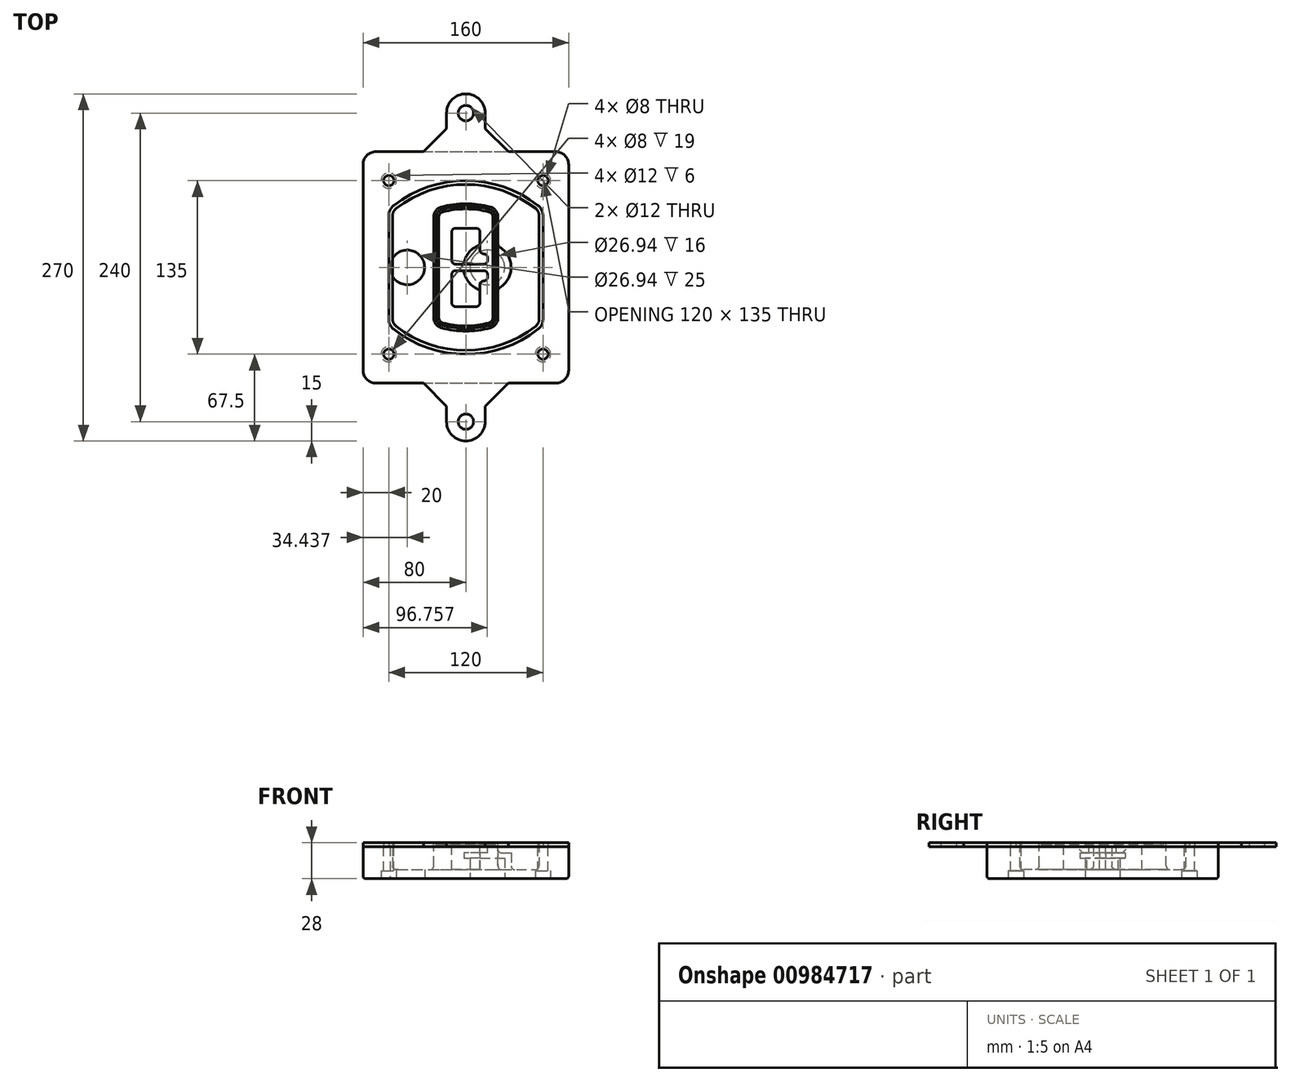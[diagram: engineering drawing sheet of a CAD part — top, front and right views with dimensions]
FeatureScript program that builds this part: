
annotation { "Feature Type Name" : "Feature", "Feature Type Description" : "" }
export const myFeature = defineFeature(function(context is Context, id is Id, definition is map)
    precondition{}
    {
        {
            var Q0;
            Q0=qCreatedBy(makeId("Top.planeOp"),FACE);
            var sketch = newSketch(context, id + "F0", { "sketchPlane" : qUnion([Q0])});
            skPoint(sketch, "E0.rect.middle", {"position": v(0, 0) * mm});
            skLineSegment(sketch, "E1.bottom", {"start": v(-70, -90) * mm, "end": v(70, -90) * mm});
            skLineSegment(sketch, "E1.top", {"start": v(-70, 90) * mm, "end": v(70, 90) * mm});
            skLineSegment(sketch, "E1.left", {"start": v(-80, -80) * mm, "end": v(-80, 80) * mm});
            skLineSegment(sketch, "E1.right", {"start": v(80, -80) * mm, "end": v(80, 80) * mm});
            skLineSegment(sketch, "E2", {"start": v(-80, 90) * mm, "end": v(80, -90) * mm, "construction": true});
            skLineSegment(sketch, "E3", {"start": v(80, 90) * mm, "end": v(-80, -90) * mm, "construction": true});
            skCircle(sketch, "E4", {"center": v(-60, 67.5) * mm, "radius": 4 * mm});
            skCircle(sketch, "E5", {"center": v(60, 67.5) * mm, "radius": 4 * mm});
            skCircle(sketch, "E6", {"center": v(60, -67.5) * mm, "radius": 4 * mm});
            skCircle(sketch, "E7", {"center": v(-60, -67.5) * mm, "radius": 4 * mm});
            skLineSegment(sketch, "E8", {"start": v(-60, 67.5) * mm, "end": v(60, 67.5) * mm, "construction": true});
            skLineSegment(sketch, "E9", {"start": v(60, 67.5) * mm, "end": v(60, -67.5) * mm, "construction": true});
            skLineSegment(sketch, "E10", {"start": v(60, -67.5) * mm, "end": v(-60, -67.5) * mm, "construction": true});
            skLineSegment(sketch, "E11", {"start": v(-60, -67.5) * mm, "end": v(-60, 67.5) * mm, "construction": true});
            skLineSegment(sketch, "E12", {"start": v(-60, 40.3) * mm, "end": v(-60, -40.3) * mm});
            skLineSegment(sketch, "E13", {"start": v(60, 40.3) * mm, "end": v(60, -40.3) * mm});
            skArc(sketch, "E14", {"start": v(56.15, 48.18) * mm, "mid": v(0, 67.5) * mm, "end": v(-56.15, 48.18) * mm});
            skArc(sketch, "E15", {"start": v(-56.15, -48.18) * mm, "mid": v(0, -67.5) * mm, "end": v(56.15, -48.18) * mm});
            skLineSegment(sketch, "E16", {"start": v(-60, 0) * mm, "end": v(60, 0) * mm, "construction": true});
            skPoint(sketch, "E17.visualSharp", {"position": v(-60, -45) * mm});
            skArc(sketch, "E17.filletArc", {"start": v(-60, -40.3) * mm, "mid": v(-58.99, -44.68) * mm, "end": v(-56.15, -48.18) * mm});
            skPoint(sketch, "E18.visualSharp", {"position": v(-60, 45) * mm});
            skArc(sketch, "E18.filletArc", {"start": v(-56.15, 48.18) * mm, "mid": v(-58.99, 44.68) * mm, "end": v(-60, 40.3) * mm});
            skPoint(sketch, "E19.visualSharp", {"position": v(60, 45) * mm});
            skArc(sketch, "E19.filletArc", {"start": v(60, 40.3) * mm, "mid": v(58.99, 44.68) * mm, "end": v(56.15, 48.18) * mm});
            skPoint(sketch, "E20.visualSharp", {"position": v(60, -45) * mm});
            skArc(sketch, "E20.filletArc", {"start": v(56.15, -48.18) * mm, "mid": v(58.99, -44.68) * mm, "end": v(60, -40.3) * mm});
            skPoint(sketch, "E21.visualSharp", {"position": v(-80, 90) * mm});
            skArc(sketch, "E21.filletArc", {"start": v(-70, 90) * mm, "mid": v(-77.07, 87.07) * mm, "end": v(-80, 80) * mm});
            skPoint(sketch, "E22.visualSharp", {"position": v(80, 90) * mm});
            skArc(sketch, "E22.filletArc", {"start": v(80, 80) * mm, "mid": v(77.07, 87.07) * mm, "end": v(70, 90) * mm});
            skPoint(sketch, "E23.visualSharp", {"position": v(80, -90) * mm});
            skArc(sketch, "E23.filletArc", {"start": v(70, -90) * mm, "mid": v(77.07, -87.07) * mm, "end": v(80, -80) * mm});
            skPoint(sketch, "E24.visualSharp", {"position": v(-80, -90) * mm});
            skArc(sketch, "E24.filletArc", {"start": v(-80, -80) * mm, "mid": v(-77.07, -87.07) * mm, "end": v(-70, -90) * mm});
            skArc(sketch, "E25.0", {"start": v(57, 40.3) * mm, "mid": v(56.3, 43.36) * mm, "end": v(54.3, 45.81) * mm});
            skLineSegment(sketch, "E25.1", {"start": v(57, 40.3) * mm, "end": v(57, -40.3) * mm});
            skArc(sketch, "E25.2", {"start": v(54.3, -45.81) * mm, "mid": v(56.3, -43.36) * mm, "end": v(57, -40.3) * mm});
            skArc(sketch, "E25.3", {"start": v(-54.3, -45.81) * mm, "mid": v(0, -64.5) * mm, "end": v(54.3, -45.81) * mm});
            skArc(sketch, "E25.4", {"start": v(-57, -40.3) * mm, "mid": v(-56.3, -43.36) * mm, "end": v(-54.3, -45.81) * mm});
            skArc(sketch, "E25.5", {"start": v(54.3, 45.81) * mm, "mid": v(0, 64.5) * mm, "end": v(-54.3, 45.81) * mm});
            skLineSegment(sketch, "E25.6", {"start": v(-57, 40.3) * mm, "end": v(-57, -40.3) * mm});
            skArc(sketch, "E25.7", {"start": v(-54.3, 45.81) * mm, "mid": v(-56.3, 43.36) * mm, "end": v(-57, 40.3) * mm});
            skArc(sketch, "E26.0", {"start": v(-58.62, 51.33) * mm, "mid": v(-62.58, 46.43) * mm, "end": v(-64, 40.3) * mm});
            skArc(sketch, "E26.1", {"start": v(58.62, 51.33) * mm, "mid": v(0, 71.5) * mm, "end": v(-58.62, 51.33) * mm});
            skArc(sketch, "E26.2", {"start": v(64, 40.3) * mm, "mid": v(62.58, 46.43) * mm, "end": v(58.62, 51.33) * mm});
            skLineSegment(sketch, "E26.3", {"start": v(64, 40.3) * mm, "end": v(64, -40.3) * mm});
            skArc(sketch, "E26.4", {"start": v(58.62, -51.33) * mm, "mid": v(62.58, -46.43) * mm, "end": v(64, -40.3) * mm});
            skLineSegment(sketch, "E26.5", {"start": v(-64, 40.3) * mm, "end": v(-64, -40.3) * mm});
            skArc(sketch, "E26.6", {"start": v(-58.62, -51.33) * mm, "mid": v(0, -71.5) * mm, "end": v(58.62, -51.33) * mm});
            skArc(sketch, "E26.7", {"start": v(-64, -40.3) * mm, "mid": v(-62.58, -46.43) * mm, "end": v(-58.62, -51.33) * mm});
            skSolve(sketch);
        }
        {
            var Q0;
            Q0=makeQuery(id+"F0.imprint","IMPRINT",FACE,{"disambiguationData":[TD([[makeQuery(id+"F0.imprint","IMPRINT",EDGE,{"derivedFrom":sQuery(id+"F0.wireOp",EDGE,"E1.bottom")}),1.0]])]});
            var Q1;
            Q1=makeQuery(id+"F0.imprint","IMPRINT",FACE,{"disambiguationData":[TD([[makeQuery(id+"F0.imprint","IMPRINT",EDGE,{"derivedFrom":sQuery(id+"F0.wireOp",EDGE,"E12")}),1.0]])]});
            var Q2;
            Q2=makeQuery(id+"F0.imprint","IMPRINT",FACE,{"disambiguationData":[TD([[makeQuery(id+"F0.imprint","IMPRINT",EDGE,{"derivedFrom":sQuery(id+"F0.wireOp",EDGE,"E25.0")}),1.0]])]});
            var Q3;
            Q3=makeQuery(id+"F0.imprint","IMPRINT",FACE,{"disambiguationData":[TD([[makeQuery(id+"F0.imprint","IMPRINT",EDGE,{"derivedFrom":sQuery(id+"F0.wireOp",EDGE,"E12")}),-1.0]])]});
            extrude(context, id + "F1", {"entities" : qUnion([Q0, Q1, Q2, Q3]), "oppositeDirection" : true, "depth" : 25 * mm});
        }
        {
            var Q0;
            Q0=makeQuery(id+"F0.imprint","IMPRINT",FACE,{"disambiguationData":[TD([[makeQuery(id+"F0.imprint","IMPRINT",EDGE,{"derivedFrom":sQuery(id+"F0.wireOp",EDGE,"E12")}),1.0]])]});
            extrude(context, id + "F2", {"entities" : qUnion([Q0]), "operationType" : NewBodyOperationType.ADD, "depth" : 3 * mm});
        }
        {
            var Q0;
            Q0=makeQuery(id+"F0.imprint","IMPRINT",FACE,{"disambiguationData":[TD([[makeQuery(id+"F0.imprint","IMPRINT",EDGE,{"derivedFrom":sQuery(id+"F0.wireOp",EDGE,"E25.0")}),1.0]])]});
            extrude(context, id + "F3", {"entities" : qUnion([Q0]), "operationType" : NewBodyOperationType.REMOVE, "oppositeDirection" : true, "depth" : 18 * mm});
        }
        {
            var Q0;
            Q0=makeQuery(id+"F2.opExtrude","CAP_FACE",FACE,{"disambiguationData":[OSD([sQuery(id+"F0.wireOp",EDGE,"E12"),sQuery(id+"F0.wireOp",EDGE,"E13"),sQuery(id+"F0.wireOp",EDGE,"E14"),sQuery(id+"F0.wireOp",EDGE,"E15"),sQuery(id+"F0.wireOp",EDGE,"E17.filletArc"),sQuery(id+"F0.wireOp",EDGE,"E18.filletArc"),sQuery(id+"F0.wireOp",EDGE,"E19.filletArc"),sQuery(id+"F0.wireOp",EDGE,"E20.filletArc"),sQuery(id+"F0.wireOp",EDGE,"E25.0"),sQuery(id+"F0.wireOp",EDGE,"E25.1"),sQuery(id+"F0.wireOp",EDGE,"E25.2"),sQuery(id+"F0.wireOp",EDGE,"E25.3"),sQuery(id+"F0.wireOp",EDGE,"E25.4"),sQuery(id+"F0.wireOp",EDGE,"E25.5"),sQuery(id+"F0.wireOp",EDGE,"E25.6"),sQuery(id+"F0.wireOp",EDGE,"E25.7")])],"isStart":false});
            var sketch = newSketch(context, id + "F4", { "sketchPlane" : qUnion([Q0])});
            skArc(sketch, "E27.0", {"start": v(-19.08, -46.97) * mm, "mid": v(0, -49.5) * mm, "end": v(19.08, -46.97) * mm});
            skArc(sketch, "E28.0", {"start": v(19.08, 46.97) * mm, "mid": v(0, 49.5) * mm, "end": v(-19.08, 46.97) * mm});
            skLineSegment(sketch, "E29", {"start": v(-25, 39.25) * mm, "end": v(-25, -39.25) * mm});
            skLineSegment(sketch, "E30", {"start": v(25, 39.25) * mm, "end": v(25, -39.25) * mm});
            skLineSegment(sketch, "E31", {"start": v(-25, 45.1) * mm, "end": v(25, 45.1) * mm, "construction": true});
            skLineSegment(sketch, "E32", {"start": v(-25, -45.1) * mm, "end": v(25, -45.1) * mm, "construction": true});
            skPoint(sketch, "E33.visualSharp", {"position": v(-25, 45.1) * mm});
            skArc(sketch, "E33.filletArc", {"start": v(-19.08, 46.97) * mm, "mid": v(-23.35, 44.11) * mm, "end": v(-25, 39.25) * mm});
            skPoint(sketch, "E34.visualSharp", {"position": v(25, 45.1) * mm});
            skArc(sketch, "E34.filletArc", {"start": v(25, 39.25) * mm, "mid": v(23.35, 44.11) * mm, "end": v(19.08, 46.97) * mm});
            skPoint(sketch, "E35.visualSharp", {"position": v(25, -45.1) * mm});
            skArc(sketch, "E35.filletArc", {"start": v(19.08, -46.97) * mm, "mid": v(23.35, -44.11) * mm, "end": v(25, -39.25) * mm});
            skPoint(sketch, "E36.visualSharp", {"position": v(-25, -45.1) * mm});
            skArc(sketch, "E36.filletArc", {"start": v(-25, -39.25) * mm, "mid": v(-23.35, -44.11) * mm, "end": v(-19.08, -46.97) * mm});
            skArc(sketch, "E37.0", {"start": v(54.3, 45.81) * mm, "mid": v(0, 64.5) * mm, "end": v(-54.3, 45.81) * mm});
            skArc(sketch, "E37.1", {"start": v(-54.3, 45.81) * mm, "mid": v(-56.3, 43.36) * mm, "end": v(-57, 40.3) * mm});
            skLineSegment(sketch, "E37.2", {"start": v(-57, 40.3) * mm, "end": v(-57, -40.3) * mm});
            skArc(sketch, "E37.3", {"start": v(-57, -40.3) * mm, "mid": v(-56.3, -43.36) * mm, "end": v(-54.3, -45.81) * mm});
            skArc(sketch, "E37.4", {"start": v(-54.3, -45.81) * mm, "mid": v(0, -64.5) * mm, "end": v(54.3, -45.81) * mm});
            skArc(sketch, "E37.5", {"start": v(54.3, -45.81) * mm, "mid": v(56.3, -43.36) * mm, "end": v(57, -40.3) * mm});
            skLineSegment(sketch, "E37.6", {"start": v(57, 40.3) * mm, "end": v(57, -40.3) * mm});
            skArc(sketch, "E37.7", {"start": v(57, 40.3) * mm, "mid": v(56.3, 43.36) * mm, "end": v(54.3, 45.81) * mm});
            skLineSegment(sketch, "E38.0", {"start": v(23, 39.25) * mm, "end": v(23, -39.25) * mm});
            skArc(sketch, "E38.1", {"start": v(18.56, -45.04) * mm, "mid": v(21.76, -42.9) * mm, "end": v(23, -39.25) * mm});
            skArc(sketch, "E38.2", {"start": v(-18.56, -45.04) * mm, "mid": v(0, -47.5) * mm, "end": v(18.56, -45.04) * mm});
            skArc(sketch, "E38.3", {"start": v(-23, -39.25) * mm, "mid": v(-21.76, -42.9) * mm, "end": v(-18.56, -45.04) * mm});
            skLineSegment(sketch, "E38.4", {"start": v(-23, 39.25) * mm, "end": v(-23, -39.25) * mm});
            skArc(sketch, "E38.5", {"start": v(23, 39.25) * mm, "mid": v(21.76, 42.9) * mm, "end": v(18.56, 45.04) * mm});
            skArc(sketch, "E38.6", {"start": v(-18.56, 45.04) * mm, "mid": v(-21.76, 42.9) * mm, "end": v(-23, 39.25) * mm});
            skArc(sketch, "E38.7", {"start": v(18.56, 45.04) * mm, "mid": v(0, 47.5) * mm, "end": v(-18.56, 45.04) * mm});
            skArc(sketch, "E39.0", {"start": v(21, 39.25) * mm, "mid": v(20.18, 41.68) * mm, "end": v(18.04, 43.1) * mm});
            skLineSegment(sketch, "E39.1", {"start": v(21, 39.25) * mm, "end": v(21, -39.25) * mm});
            skArc(sketch, "E39.2", {"start": v(18.04, -43.1) * mm, "mid": v(20.18, -41.68) * mm, "end": v(21, -39.25) * mm});
            skArc(sketch, "E39.3", {"start": v(-18.04, -43.1) * mm, "mid": v(0, -45.5) * mm, "end": v(18.04, -43.1) * mm});
            skArc(sketch, "E39.4", {"start": v(-21, -39.25) * mm, "mid": v(-20.18, -41.68) * mm, "end": v(-18.04, -43.1) * mm});
            skArc(sketch, "E39.5", {"start": v(18.04, 43.1) * mm, "mid": v(0, 45.5) * mm, "end": v(-18.04, 43.1) * mm});
            skLineSegment(sketch, "E39.6", {"start": v(-21, 39.25) * mm, "end": v(-21, -39.25) * mm});
            skArc(sketch, "E39.7", {"start": v(-18.04, 43.1) * mm, "mid": v(-20.18, 41.68) * mm, "end": v(-21, 39.25) * mm});
            skLineSegment(sketch, "E40", {"start": v(-25, 0) * mm, "end": v(25, 0) * mm, "construction": true});
            skLineSegment(sketch, "E41", {"start": v(-11, 5.5) * mm, "end": v(-11, 27.5) * mm});
            skLineSegment(sketch, "E42", {"start": v(-8, 30.5) * mm, "end": v(8, 30.5) * mm});
            skLineSegment(sketch, "E43", {"start": v(11, 27.5) * mm, "end": v(11, 13.5) * mm});
            skLineSegment(sketch, "E44", {"start": v(14, 10.5) * mm, "end": v(14, 10.5) * mm});
            skLineSegment(sketch, "E45", {"start": v(17, 7.5) * mm, "end": v(17, 5.5) * mm});
            skLineSegment(sketch, "E46", {"start": v(14, 2.5) * mm, "end": v(-8, 2.5) * mm});
            skPoint(sketch, "E47.visualSharp", {"position": v(-11, 30.5) * mm});
            skArc(sketch, "E47.filletArc", {"start": v(-8, 30.5) * mm, "mid": v(-10.12, 29.62) * mm, "end": v(-11, 27.5) * mm});
            skPoint(sketch, "E48.visualSharp", {"position": v(11, 30.5) * mm});
            skArc(sketch, "E48.filletArc", {"start": v(11, 27.5) * mm, "mid": v(10.12, 29.62) * mm, "end": v(8, 30.5) * mm});
            skPoint(sketch, "E49.visualSharp", {"position": v(11, 10.5) * mm});
            skArc(sketch, "E49.filletArc", {"start": v(11, 13.5) * mm, "mid": v(11.88, 11.38) * mm, "end": v(14, 10.5) * mm});
            skPoint(sketch, "E50.visualSharp", {"position": v(17, 10.5) * mm});
            skArc(sketch, "E50.filletArc", {"start": v(17, 7.5) * mm, "mid": v(16.12, 9.62) * mm, "end": v(14, 10.5) * mm});
            skPoint(sketch, "E51.visualSharp", {"position": v(17, 2.5) * mm});
            skArc(sketch, "E51.filletArc", {"start": v(14, 2.5) * mm, "mid": v(16.12, 3.38) * mm, "end": v(17, 5.5) * mm});
            skPoint(sketch, "E52.visualSharp", {"position": v(-11, 2.5) * mm});
            skArc(sketch, "E52.filletArc", {"start": v(-11, 5.5) * mm, "mid": v(-10.12, 3.38) * mm, "end": v(-8, 2.5) * mm});
            skLineSegment(sketch, "E53.0.MirrorCS", {"start": v(14, -2.5) * mm, "end": v(-8, -2.5) * mm});
            skArc(sketch, "E54.0.MirrorCS", {"start": v(-11, -5.5) * mm, "mid": v(-10.12, -3.38) * mm, "end": v(-8, -2.5) * mm});
            skLineSegment(sketch, "E55.0.MirrorCS", {"start": v(-11, -5.5) * mm, "end": v(-11, -27.5) * mm});
            skArc(sketch, "E56.0.MirrorCS", {"start": v(-8, -30.5) * mm, "mid": v(-10.12, -29.62) * mm, "end": v(-11, -27.5) * mm});
            skLineSegment(sketch, "E57.0.MirrorCS", {"start": v(-8, -30.5) * mm, "end": v(8, -30.5) * mm});
            skArc(sketch, "E58.0.MirrorCS", {"start": v(11, -27.5) * mm, "mid": v(10.12, -29.62) * mm, "end": v(8, -30.5) * mm});
            skLineSegment(sketch, "E59.0.MirrorCS", {"start": v(11, -27.5) * mm, "end": v(11, -13.5) * mm});
            skArc(sketch, "E60.0.MirrorCS", {"start": v(11, -13.5) * mm, "mid": v(11.88, -11.38) * mm, "end": v(14, -10.5) * mm});
            skArc(sketch, "E61.0.MirrorCS", {"start": v(17, -7.5) * mm, "mid": v(16.12, -9.62) * mm, "end": v(14, -10.5) * mm});
            skLineSegment(sketch, "E62.0.MirrorCS", {"start": v(17, -7.5) * mm, "end": v(17, -5.5) * mm});
            skArc(sketch, "E63.0.MirrorCS", {"start": v(14, -2.5) * mm, "mid": v(16.12, -3.38) * mm, "end": v(17, -5.5) * mm});
            skSolve(sketch);
        }
        {
            var Q0;
            Q0=makeQuery(id+"F4.imprint","IMPRINT",FACE,{"disambiguationData":[TD([[makeQuery(id+"F4.imprint","IMPRINT",EDGE,{"derivedFrom":sQuery(id+"F4.wireOp",EDGE,"E27.0")}),1.0]])]});
            var Q1;
            Q1=makeQuery(id+"F4.imprint","IMPRINT",FACE,{"disambiguationData":[TD([[makeQuery(id+"F4.imprint","IMPRINT",EDGE,{"derivedFrom":sQuery(id+"F4.wireOp",EDGE,"E38.0")}),-1.0]])]});
            var Q2;
            Q2=makeQuery(id+"F4.imprint","IMPRINT",FACE,{"disambiguationData":[TD([[makeQuery(id+"F4.imprint","IMPRINT",EDGE,{"derivedFrom":sQuery(id+"F4.wireOp",EDGE,"E39.0")}),1.0]])]});
            extrude(context, id + "F5", {"entities" : qUnion([Q0, Q1, Q2]), "operationType" : NewBodyOperationType.ADD, "endBound" : BoundingType.UP_TO_NEXT, "oppositeDirection" : true, "depth" : 25 * mm});
        }
        {
            var Q0;
            Q0=makeQuery(id+"F4.imprint","IMPRINT",FACE,{"disambiguationData":[TD([[makeQuery(id+"F4.imprint","IMPRINT",EDGE,{"derivedFrom":sQuery(id+"F4.wireOp",EDGE,"E38.0")}),-1.0]])]});
            extrude(context, id + "F6", {"entities" : qUnion([Q0]), "operationType" : NewBodyOperationType.REMOVE, "oppositeDirection" : true, "depth" : 2 * mm});
        }
        {
            var Q0;
            Q0=makeQuery(id+"F1.opExtrude","CAP_FACE",FACE,{"disambiguationData":[OSD([sQuery(id+"F0.wireOp",EDGE,"E1.bottom"),sQuery(id+"F0.wireOp",EDGE,"E1.top"),sQuery(id+"F0.wireOp",EDGE,"E1.left"),sQuery(id+"F0.wireOp",EDGE,"E1.right"),sQuery(id+"F0.wireOp",EDGE,"E4"),sQuery(id+"F0.wireOp",EDGE,"E5"),sQuery(id+"F0.wireOp",EDGE,"E6"),sQuery(id+"F0.wireOp",EDGE,"E7"),sQuery(id+"F0.wireOp",EDGE,"E21.filletArc"),sQuery(id+"F0.wireOp",EDGE,"E22.filletArc"),sQuery(id+"F0.wireOp",EDGE,"E23.filletArc"),sQuery(id+"F0.wireOp",EDGE,"E24.filletArc")])],"isStart":false});
            var sketch = newSketch(context, id + "F7", { "sketchPlane" : qUnion([Q0])});
            skCircle(sketch, "E64", {"center": v(16.76, 0) * mm, "radius": 13.47 * mm});
            skCircle(sketch, "E65", {"center": v(-45.56, 0) * mm, "radius": 13.47 * mm});
            skLineSegment(sketch, "E66", {"start": v(80, 0) * mm, "end": v(-80, 0) * mm});
            skCircle(sketch, "E67", {"center": v(16.76, 0) * mm, "radius": 18.47 * mm});
            skCircle(sketch, "E68", {"center": v(60, -67.5) * mm, "radius": 6 * mm});
            skCircle(sketch, "E69", {"center": v(-60, -67.5) * mm, "radius": 6 * mm});
            skCircle(sketch, "E70", {"center": v(-60, 67.5) * mm, "radius": 6 * mm});
            skCircle(sketch, "E71", {"center": v(60, 67.5) * mm, "radius": 6 * mm});
            skSolve(sketch);
        }
        {
            var Q0;
            {var subQ1=sQuery(id+"F7.wireOp",EDGE,"E66");var subQ4=sQuery(id+"F7.wireOp",EDGE,"E64");var subQ6=makeQuery(id+"F7.imprint","INTERSECT",VERTEX,{"disambiguationData":[OD(0.0)],"derivedFrom":[subQ4,subQ1]});Q0=makeQuery(id+"F7.imprint","IMPRINT",FACE,{"disambiguationData":[TD([[makeQuery(id+"F7.imprint","IMPRINT",EDGE,{"disambiguationData":[TD([[subQ6,-1.0]])],"derivedFrom":subQ4}),-1.0]])]});}
            var Q1;
            {var subQ0=sQuery(id+"F7.wireOp",EDGE,"E66");var subQ1=sQuery(id+"F7.wireOp",EDGE,"E64");var subQ3=makeQuery(id+"F7.imprint","INTERSECT",VERTEX,{"disambiguationData":[OD(0.0)],"derivedFrom":[subQ1,subQ0]});Q1=makeQuery(id+"F7.imprint","IMPRINT",FACE,{"disambiguationData":[TD([[makeQuery(id+"F7.imprint","IMPRINT",EDGE,{"disambiguationData":[TD([[subQ3,-1.0]])],"derivedFrom":subQ1}),1.0]])]});}
            var Q2;
            {var subQ0=sQuery(id+"F7.wireOp",EDGE,"E66");var subQ1=sQuery(id+"F7.wireOp",EDGE,"E64");var subQ3=makeQuery(id+"F7.imprint","INTERSECT",VERTEX,{"disambiguationData":[OD(0.0)],"derivedFrom":[subQ1,subQ0]});Q2=makeQuery(id+"F7.imprint","IMPRINT",FACE,{"disambiguationData":[TD([[makeQuery(id+"F7.imprint","IMPRINT",EDGE,{"disambiguationData":[TD([[subQ3,1.0]])],"derivedFrom":subQ1}),1.0]])]});}
            var Q3;
            {var subQ1=sQuery(id+"F7.wireOp",EDGE,"E66");var subQ4=sQuery(id+"F7.wireOp",EDGE,"E64");var subQ6=makeQuery(id+"F7.imprint","INTERSECT",VERTEX,{"disambiguationData":[OD(0.0)],"derivedFrom":[subQ4,subQ1]});Q3=makeQuery(id+"F7.imprint","IMPRINT",FACE,{"disambiguationData":[TD([[makeQuery(id+"F7.imprint","IMPRINT",EDGE,{"disambiguationData":[TD([[subQ6,1.0]])],"derivedFrom":subQ4}),-1.0]])]});}
            extrude(context, id + "F8", {"entities" : qUnion([Q0, Q1, Q2, Q3]), "operationType" : NewBodyOperationType.ADD, "oppositeDirection" : true, "depth" : 20 * mm});
        }
        {
            var Q0;
            {var subQ0=sQuery(id+"F7.wireOp",EDGE,"E66");var subQ1=sQuery(id+"F7.wireOp",EDGE,"E64");var subQ3=makeQuery(id+"F7.imprint","INTERSECT",VERTEX,{"disambiguationData":[OD(0.0)],"derivedFrom":[subQ1,subQ0]});Q0=makeQuery(id+"F7.imprint","IMPRINT",FACE,{"disambiguationData":[TD([[makeQuery(id+"F7.imprint","IMPRINT",EDGE,{"disambiguationData":[TD([[subQ3,-1.0]])],"derivedFrom":subQ1}),1.0]])]});}
            var Q1;
            {var subQ0=sQuery(id+"F7.wireOp",EDGE,"E66");var subQ1=sQuery(id+"F7.wireOp",EDGE,"E64");var subQ3=makeQuery(id+"F7.imprint","INTERSECT",VERTEX,{"disambiguationData":[OD(0.0)],"derivedFrom":[subQ1,subQ0]});Q1=makeQuery(id+"F7.imprint","IMPRINT",FACE,{"disambiguationData":[TD([[makeQuery(id+"F7.imprint","IMPRINT",EDGE,{"disambiguationData":[TD([[subQ3,1.0]])],"derivedFrom":subQ1}),1.0]])]});}
            extrude(context, id + "F9", {"entities" : qUnion([Q0, Q1]), "operationType" : NewBodyOperationType.REMOVE, "oppositeDirection" : true, "depth" : 16 * mm});
        }
        {
            var Q0;
            {var subQ0=sQuery(id+"F7.wireOp",EDGE,"E66");var subQ1=sQuery(id+"F7.wireOp",EDGE,"E65");var subQ3=makeQuery(id+"F7.imprint","INTERSECT",VERTEX,{"disambiguationData":[OD(0.0)],"derivedFrom":[subQ1,subQ0]});Q0=makeQuery(id+"F7.imprint","IMPRINT",FACE,{"disambiguationData":[TD([[makeQuery(id+"F7.imprint","IMPRINT",EDGE,{"disambiguationData":[TD([[subQ3,-1.0]])],"derivedFrom":subQ1}),1.0]])]});}
            var Q1;
            {var subQ0=sQuery(id+"F7.wireOp",EDGE,"E66");var subQ1=sQuery(id+"F7.wireOp",EDGE,"E65");var subQ3=makeQuery(id+"F7.imprint","INTERSECT",VERTEX,{"disambiguationData":[OD(0.0)],"derivedFrom":[subQ1,subQ0]});Q1=makeQuery(id+"F7.imprint","IMPRINT",FACE,{"disambiguationData":[TD([[makeQuery(id+"F7.imprint","IMPRINT",EDGE,{"disambiguationData":[TD([[subQ3,1.0]])],"derivedFrom":subQ1}),1.0]])]});}
            extrude(context, id + "F10", {"entities" : qUnion([Q0, Q1]), "operationType" : NewBodyOperationType.REMOVE, "oppositeDirection" : true, "depth" : 25 * mm});
        }
        {
            var Q0;
            Q0=makeQuery(id+"F7.imprint","IMPRINT",FACE,{"disambiguationData":[TD([[makeQuery(id+"F7.imprint","IMPRINT",EDGE,{"derivedFrom":sQuery(id+"F7.wireOp",EDGE,"E68")}),1.0]])]});
            var Q1;
            Q1=makeQuery(id+"F7.imprint","IMPRINT",FACE,{"disambiguationData":[TD([[makeQuery(id+"F7.imprint","IMPRINT",EDGE,{"derivedFrom":makeQuery(id+"F1.opExtrude","CAP_EDGE",EDGE,{"disambiguationData":[OSD([sQuery(id+"F0.wireOp",EDGE,"E5")])],"isStart":false})}),-1.0]])]});
            var Q2;
            Q2=makeQuery(id+"F7.imprint","IMPRINT",FACE,{"disambiguationData":[TD([[makeQuery(id+"F7.imprint","IMPRINT",EDGE,{"derivedFrom":sQuery(id+"F7.wireOp",EDGE,"E69")}),1.0]])]});
            var Q3;
            Q3=makeQuery(id+"F7.imprint","IMPRINT",FACE,{"disambiguationData":[TD([[makeQuery(id+"F7.imprint","IMPRINT",EDGE,{"derivedFrom":makeQuery(id+"F1.opExtrude","CAP_EDGE",EDGE,{"disambiguationData":[OSD([sQuery(id+"F0.wireOp",EDGE,"E4")])],"isStart":false})}),-1.0]])]});
            var Q4;
            Q4=makeQuery(id+"F7.imprint","IMPRINT",FACE,{"disambiguationData":[TD([[makeQuery(id+"F7.imprint","IMPRINT",EDGE,{"derivedFrom":sQuery(id+"F7.wireOp",EDGE,"E70")}),1.0]])]});
            var Q5;
            Q5=makeQuery(id+"F7.imprint","IMPRINT",FACE,{"disambiguationData":[TD([[makeQuery(id+"F7.imprint","IMPRINT",EDGE,{"derivedFrom":makeQuery(id+"F1.opExtrude","CAP_EDGE",EDGE,{"disambiguationData":[OSD([sQuery(id+"F0.wireOp",EDGE,"E7")])],"isStart":false})}),-1.0]])]});
            var Q6;
            Q6=makeQuery(id+"F7.imprint","IMPRINT",FACE,{"disambiguationData":[TD([[makeQuery(id+"F7.imprint","IMPRINT",EDGE,{"derivedFrom":sQuery(id+"F7.wireOp",EDGE,"E71")}),1.0]])]});
            var Q7;
            Q7=makeQuery(id+"F7.imprint","IMPRINT",FACE,{"disambiguationData":[TD([[makeQuery(id+"F7.imprint","IMPRINT",EDGE,{"derivedFrom":makeQuery(id+"F1.opExtrude","CAP_EDGE",EDGE,{"disambiguationData":[OSD([sQuery(id+"F0.wireOp",EDGE,"E6")])],"isStart":false})}),-1.0]])]});
            extrude(context, id + "F11", {"entities" : qUnion([Q0, Q1, Q2, Q3, Q4, Q5, Q6, Q7]), "operationType" : NewBodyOperationType.REMOVE, "oppositeDirection" : true, "depth" : 6 * mm});
        }
        {
            var Q0;
            Q0=makeQuery(id+"F9.boolean.opBoolean","COPY",FACE,{"derivedFrom":makeQuery(id+"F9.opExtrude","CAP_FACE",FACE,{"disambiguationData":[OSD([sQuery(id+"F7.wireOp",EDGE,"E64")])],"isStart":false})});
            var sketch = newSketch(context, id + "F12", { "sketchPlane" : qUnion([Q0])});
            skArc(sketch, "E72.0", {"start": v(11, 17.55) * mm, "mid": v(2.57, 11.82) * mm, "end": v(-1.54, 2.5) * mm});
            skArc(sketch, "E72.1", {"start": v(-1.54, -2.5) * mm, "mid": v(2.57, -11.82) * mm, "end": v(11, -17.55) * mm});
            skLineSegment(sketch, "E73", {"start": v(-1.54, -2.5) * mm, "end": v(14, -2.5) * mm});
            skLineSegment(sketch, "E74.0", {"start": v(14, 2.5) * mm, "end": v(-1.54, 2.5) * mm});
            skArc(sketch, "E74.1", {"start": v(14, 2.5) * mm, "mid": v(16.12, 3.38) * mm, "end": v(17, 5.5) * mm});
            skLineSegment(sketch, "E74.2", {"start": v(17, 7.5) * mm, "end": v(17, 5.5) * mm});
            skArc(sketch, "E74.3", {"start": v(17, 7.5) * mm, "mid": v(16.12, 9.62) * mm, "end": v(14, 10.5) * mm});
            skArc(sketch, "E74.4", {"start": v(11, 13.5) * mm, "mid": v(11.88, 11.38) * mm, "end": v(14, 10.5) * mm});
            skLineSegment(sketch, "E74.5", {"start": v(11, 17.55) * mm, "end": v(11, 13.5) * mm});
            skLineSegment(sketch, "E74.7", {"start": v(14, -2.5) * mm, "end": v(-1.54, -2.5) * mm});
            skArc(sketch, "E74.8", {"start": v(14, -2.5) * mm, "mid": v(16.12, -3.38) * mm, "end": v(17, -5.5) * mm});
            skLineSegment(sketch, "E74.9", {"start": v(17, -7.5) * mm, "end": v(17, -5.5) * mm});
            skArc(sketch, "E74.10", {"start": v(17, -7.5) * mm, "mid": v(16.12, -9.62) * mm, "end": v(14, -10.5) * mm});
            skArc(sketch, "E74.11", {"start": v(11, -13.5) * mm, "mid": v(11.88, -11.38) * mm, "end": v(14, -10.5) * mm});
            skLineSegment(sketch, "E74.12", {"start": v(11, -17.55) * mm, "end": v(11, -13.5) * mm});
            skPoint(sketch, "E75.orphan", {"position": v(11, -27.5) * mm});
            skPoint(sketch, "E76.orphan", {"position": v(-8, -2.5) * mm});
            skPoint(sketch, "E77.orphan", {"position": v(-8, 2.5) * mm});
            skPoint(sketch, "E78.orphan", {"position": v(11, 27.5) * mm});
            skSolve(sketch);
        }
        {
            var Q0;
            {var subQ7=sQuery(id+"F12.wireOp",EDGE,"E72.0");var subQ14=sQuery(id+"F12.wireOp",EDGE,"E72.1");var subQ16=sQuery(id+"F12.wireOp",EDGE,"E74.1");var subQ18=sQuery(id+"F12.wireOp",EDGE,"E74.8");Q0=qUnion([makeQuery(id+"F12.imprint","IMPRINT",FACE,{"disambiguationData":[TD([[makeQuery(id+"F12.imprint","IMPRINT",EDGE,{"derivedFrom":subQ7}),1.0]])]}),makeQuery(id+"F12.imprint","IMPRINT",FACE,{"disambiguationData":[TD([[makeQuery(id+"F12.imprint","IMPRINT",EDGE,{"derivedFrom":subQ14}),1.0]])]}),makeQuery(id+"F12.imprint","IMPRINT",FACE,{"disambiguationData":[TD([[makeQuery(id+"F12.imprint","IMPRINT",EDGE,{"derivedFrom":subQ16}),1.0]])]}),makeQuery(id+"F12.imprint","IMPRINT",FACE,{"disambiguationData":[TD([[makeQuery(id+"F12.imprint","IMPRINT",EDGE,{"derivedFrom":subQ18}),-1.0]])]})]);}
            var Q1;
            Q1=makeQuery(id+"F5.boolean.opBoolean","SPLIT",FACE,{"disambiguationData":[TD([makeQuery(id+"F5.opExtrude","SWEPT_FACE",FACE,{"disambiguationData":[OSD([sQuery(id+"F4.wireOp",EDGE,"E41")])]})])],"derivedFrom":makeQuery(id+"F3.boolean.opBoolean","COPY",FACE,{"derivedFrom":makeQuery(id+"F3.opExtrude","CAP_FACE",FACE,{"disambiguationData":[OSD([sQuery(id+"F0.wireOp",EDGE,"E25.0"),sQuery(id+"F0.wireOp",EDGE,"E25.1"),sQuery(id+"F0.wireOp",EDGE,"E25.2"),sQuery(id+"F0.wireOp",EDGE,"E25.3"),sQuery(id+"F0.wireOp",EDGE,"E25.4"),sQuery(id+"F0.wireOp",EDGE,"E25.5"),sQuery(id+"F0.wireOp",EDGE,"E25.6"),sQuery(id+"F0.wireOp",EDGE,"E25.7")])],"isStart":false})})});
            extrude(context, id + "F13", {"entities" : qUnion([Q0]), "operationType" : NewBodyOperationType.REMOVE, "endBound" : BoundingType.UP_TO_SURFACE, "endBoundEntityFace" : qUnion([Q1]), "depth" : 25 * mm});
        }
        {
            var Q0;
            Q0=makeQuery(id+"F3.boolean.opBoolean","COPY",EDGE,{"derivedFrom":makeQuery(id+"F3.opExtrude","CAP_EDGE",EDGE,{"disambiguationData":[OSD([sQuery(id+"F0.wireOp",EDGE,"E25.6")])],"isStart":false})});
            var Q1;
            Q1=makeQuery(id+"F8.boolean.opBoolean","INTERSECT",EDGE,{"derivedFrom":[makeQuery(id+"F5.opExtrude","SWEPT_FACE",FACE,{"disambiguationData":[OSD([sQuery(id+"F4.wireOp",EDGE,"E30")])]}),makeQuery(id+"F8.opExtrude","CAP_FACE",FACE,{"disambiguationData":[OSD([sQuery(id+"F7.wireOp",EDGE,"E67")])],"isStart":false})]});
            var Q2;
            Q2=makeQuery(id+"F8.boolean.opBoolean","INTERSECT",EDGE,{"disambiguationData":[OD(1.0)],"derivedFrom":[makeQuery(id+"F5.opExtrude","SWEPT_FACE",FACE,{"disambiguationData":[OSD([sQuery(id+"F4.wireOp",EDGE,"E30")])]}),makeQuery(id+"F8.opExtrude","SWEPT_FACE",FACE,{"disambiguationData":[OSD([sQuery(id+"F7.wireOp",EDGE,"E67")])]})]});
            var Q3;
            {var subQ0=sQuery(id+"F4.wireOp",EDGE,"E30");Q3=makeQuery(id+"F8.boolean.opBoolean","SPLIT",EDGE,{"disambiguationData":[TD([makeQuery(id+"F5.opExtrude","SWEPT_FACE",FACE,{"disambiguationData":[OSD([sQuery(id+"F4.wireOp",EDGE,"E35.filletArc")])]})])],"derivedFrom":makeQuery(id+"F5.opExtrude","CAP_EDGE",EDGE,{"disambiguationData":[OSD([subQ0])],"isStart":false})});}
            var Q4;
            {var subQ0=sQuery(id+"F0.wireOp",EDGE,"E25.7");var subQ1=sQuery(id+"F0.wireOp",EDGE,"E25.1");var subQ2=sQuery(id+"F0.wireOp",EDGE,"E25.6");var subQ3=sQuery(id+"F0.wireOp",EDGE,"E25.5");var subQ4=sQuery(id+"F0.wireOp",EDGE,"E25.4");var subQ5=sQuery(id+"F0.wireOp",EDGE,"E25.0");var subQ6=sQuery(id+"F0.wireOp",EDGE,"E25.2");var subQ7=sQuery(id+"F0.wireOp",EDGE,"E25.3");Q4=makeQuery(id+"F8.boolean.opBoolean","INTERSECT",EDGE,{"derivedFrom":[makeQuery(id+"F5.boolean.opBoolean","SPLIT",FACE,{"disambiguationData":[TD([makeQuery(id+"F2.opExtrude","SWEPT_FACE",FACE,{"disambiguationData":[OSD([subQ5])]})])],"derivedFrom":makeQuery(id+"F3.boolean.opBoolean","COPY",FACE,{"derivedFrom":makeQuery(id+"F3.opExtrude","CAP_FACE",FACE,{"disambiguationData":[OSD([subQ5,subQ1,subQ6,subQ7,subQ4,subQ3,subQ2,subQ0])],"isStart":false})})}),makeQuery(id+"F8.opExtrude","SWEPT_FACE",FACE,{"disambiguationData":[OSD([sQuery(id+"F7.wireOp",EDGE,"E67")])]})]});}
            var Q5;
            Q5=makeQuery(id+"F8.boolean.opBoolean","INTERSECT",EDGE,{"disambiguationData":[OD(0.0)],"derivedFrom":[makeQuery(id+"F5.opExtrude","SWEPT_FACE",FACE,{"disambiguationData":[OSD([sQuery(id+"F4.wireOp",EDGE,"E30")])]}),makeQuery(id+"F8.opExtrude","SWEPT_FACE",FACE,{"disambiguationData":[OSD([sQuery(id+"F7.wireOp",EDGE,"E67")])]})]});
            fillet(context, id + "F14", {"entities" : qUnion([Q0, Q1, Q2, Q3, Q4, Q5]), "radius" : 3 * mm, "tangentPropagation" : true, "allowEdgeOverflow" : false});
        }
        {
            var Q0;
            Q0=makeQuery(id+"F1.opExtrude","CAP_EDGE",EDGE,{"disambiguationData":[OSD([sQuery(id+"F0.wireOp",EDGE,"E1.bottom")])],"isStart":false});
            fillet(context, id + "F15", {"entities" : qUnion([Q0]), "radius" : 2 * mm, "tangentPropagation" : true, "allowEdgeOverflow" : false});
        }
        {
            var Q0;
            {var subQ0=sQuery(id+"F0.wireOp",EDGE,"E21.filletArc");var subQ1=sQuery(id+"F0.wireOp",EDGE,"E7");var subQ2=sQuery(id+"F0.wireOp",EDGE,"E6");var subQ3=sQuery(id+"F0.wireOp",EDGE,"E5");var subQ4=sQuery(id+"F0.wireOp",EDGE,"E4");var subQ5=sQuery(id+"F0.wireOp",EDGE,"E22.filletArc");var subQ6=sQuery(id+"F0.wireOp",EDGE,"E1.bottom");var subQ7=sQuery(id+"F0.wireOp",EDGE,"E1.right");var subQ8=sQuery(id+"F0.wireOp",EDGE,"E1.top");var subQ9=sQuery(id+"F0.wireOp",EDGE,"E1.left");var subQ10=sQuery(id+"F0.wireOp",EDGE,"E23.filletArc");var subQ11=sQuery(id+"F0.wireOp",EDGE,"E24.filletArc");Q0=makeQuery(id+"F2.boolean.opBoolean","SPLIT",FACE,{"disambiguationData":[TD([makeQuery(id+"F1.opExtrude","SWEPT_FACE",FACE,{"disambiguationData":[OSD([subQ6])]})])],"derivedFrom":makeQuery(id+"F1.opExtrude","CAP_FACE",FACE,{"disambiguationData":[OSD([subQ6,subQ8,subQ9,subQ7,subQ4,subQ3,subQ2,subQ1,subQ0,subQ5,subQ10,subQ11])],"isStart":true})});}
            var sketch = newSketch(context, id + "F16", { "sketchPlane" : qUnion([Q0])});
            skLineSegment(sketch, "E79.0", {"start": v(-70, 90) * mm, "end": v(70, 90) * mm});
            skArc(sketch, "E79.1", {"start": v(-70, 90) * mm, "mid": v(-77.07, 87.07) * mm, "end": v(-80, 80) * mm});
            skLineSegment(sketch, "E79.2", {"start": v(-80, -80) * mm, "end": v(-80, 80) * mm});
            skCircle(sketch, "E79.3", {"center": v(-60, 67.5) * mm, "radius": 4 * mm});
            skCircle(sketch, "E79.4", {"center": v(60, 67.5) * mm, "radius": 4 * mm});
            skArc(sketch, "E79.5", {"start": v(80, 80) * mm, "mid": v(77.07, 87.07) * mm, "end": v(70, 90) * mm});
            skLineSegment(sketch, "E79.6", {"start": v(80, -80) * mm, "end": v(80, 80) * mm});
            skArc(sketch, "E79.7", {"start": v(70, -90) * mm, "mid": v(77.07, -87.07) * mm, "end": v(80, -80) * mm});
            skLineSegment(sketch, "E79.8", {"start": v(-70, -90) * mm, "end": v(70, -90) * mm});
            skArc(sketch, "E79.9", {"start": v(-80, -80) * mm, "mid": v(-77.07, -87.07) * mm, "end": v(-70, -90) * mm});
            skCircle(sketch, "E79.10", {"center": v(-60, -67.5) * mm, "radius": 4 * mm});
            skCircle(sketch, "E79.11", {"center": v(60, -67.5) * mm, "radius": 4 * mm});
            skArc(sketch, "E79.12", {"start": v(56.15, -48.18) * mm, "mid": v(58.99, -44.68) * mm, "end": v(60, -40.3) * mm});
            skLineSegment(sketch, "E79.13", {"start": v(60, 40.3) * mm, "end": v(60, -40.3) * mm});
            skArc(sketch, "E79.14", {"start": v(-56.15, -48.18) * mm, "mid": v(0, -67.5) * mm, "end": v(56.15, -48.18) * mm});
            skArc(sketch, "E79.15", {"start": v(-60, -40.3) * mm, "mid": v(-58.99, -44.68) * mm, "end": v(-56.15, -48.18) * mm});
            skLineSegment(sketch, "E79.16", {"start": v(-60, 40.3) * mm, "end": v(-60, -40.3) * mm});
            skArc(sketch, "E79.17", {"start": v(-56.15, 48.18) * mm, "mid": v(-58.99, 44.68) * mm, "end": v(-60, 40.3) * mm});
            skArc(sketch, "E79.18", {"start": v(56.15, 48.18) * mm, "mid": v(0, 67.5) * mm, "end": v(-56.15, 48.18) * mm});
            skArc(sketch, "E79.19", {"start": v(60, 40.3) * mm, "mid": v(58.99, 44.68) * mm, "end": v(56.15, 48.18) * mm});
            skArc(sketch, "E79.20", {"start": v(56.15, 48.18) * mm, "mid": v(0, 67.5) * mm, "end": v(-56.15, 48.18) * mm});
            skLineSegment(sketch, "E80", {"start": v(0, 90) * mm, "end": v(0, 120) * mm, "construction": true});
            skCircle(sketch, "E81", {"center": v(0, 120) * mm, "radius": 6 * mm});
            skLineSegment(sketch, "E82", {"start": v(-33, 90) * mm, "end": v(-15, 108) * mm});
            skLineSegment(sketch, "E83", {"start": v(-15, 108) * mm, "end": v(-15, 120) * mm});
            skLineSegment(sketch, "E84", {"start": v(33, 90) * mm, "end": v(15, 108) * mm});
            skLineSegment(sketch, "E85", {"start": v(15, 108) * mm, "end": v(15, 120) * mm});
            skArc(sketch, "E86", {"start": v(15, 120) * mm, "mid": v(0, 135) * mm, "end": v(-15, 120) * mm});
            skLineSegment(sketch, "E87", {"start": v(-80, 0) * mm, "end": v(80, 0) * mm, "construction": true});
            skArc(sketch, "E88.MirrorCS", {"start": v(15, -120) * mm, "mid": v(0, -135) * mm, "end": v(-15, -120) * mm});
            skCircle(sketch, "E89.MirrorC", {"center": v(0, -120) * mm, "radius": 6 * mm});
            skLineSegment(sketch, "E90.MirrorCS", {"start": v(-15, -108) * mm, "end": v(-15, -120) * mm});
            skLineSegment(sketch, "E91.MirrorCS", {"start": v(-33, -90) * mm, "end": v(-15, -108) * mm});
            skLineSegment(sketch, "E92.MirrorCS", {"start": v(0, -90) * mm, "end": v(0, -120) * mm, "construction": true});
            skLineSegment(sketch, "E93.MirrorCS", {"start": v(15, -108) * mm, "end": v(15, -120) * mm});
            skLineSegment(sketch, "E94.MirrorCS", {"start": v(33, -90) * mm, "end": v(15, -108) * mm});
            skSolve(sketch);
        }
        {
            var Q0;
            Q0 = qSketchRegion(id + "F16", true);
            var Q1;
            Q1=makeQuery(id+"F2.opExtrude","CAP_FACE",FACE,{"disambiguationData":[OSD([sQuery(id+"F0.wireOp",EDGE,"E12"),sQuery(id+"F0.wireOp",EDGE,"E13"),sQuery(id+"F0.wireOp",EDGE,"E14"),sQuery(id+"F0.wireOp",EDGE,"E15"),sQuery(id+"F0.wireOp",EDGE,"E17.filletArc"),sQuery(id+"F0.wireOp",EDGE,"E18.filletArc"),sQuery(id+"F0.wireOp",EDGE,"E19.filletArc"),sQuery(id+"F0.wireOp",EDGE,"E20.filletArc"),sQuery(id+"F0.wireOp",EDGE,"E25.0"),sQuery(id+"F0.wireOp",EDGE,"E25.1"),sQuery(id+"F0.wireOp",EDGE,"E25.2"),sQuery(id+"F0.wireOp",EDGE,"E25.3"),sQuery(id+"F0.wireOp",EDGE,"E25.4"),sQuery(id+"F0.wireOp",EDGE,"E25.5"),sQuery(id+"F0.wireOp",EDGE,"E25.6"),sQuery(id+"F0.wireOp",EDGE,"E25.7")])],"isStart":false});
            extrude(context, id + "F17", {"entities" : qUnion([Q0]), "endBound" : BoundingType.UP_TO_SURFACE, "depth" : 25 * mm, "endBoundEntityFace" : qUnion([Q1]), "offsetDistance" : 25 * mm});
        }
    });
